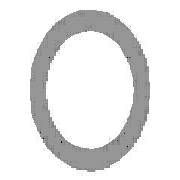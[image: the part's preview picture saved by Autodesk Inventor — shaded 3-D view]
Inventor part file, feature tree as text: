
AUTODESK INVENTOR PART (.ipt)
format: ipt  version: 2024.3 (Build 283343000, 343)  size: 120,320 bytes
history: native  units: mm (DEFAULTED — no unit token found)
features: other x4, sketch x1, plane x1
ambient origin geometry x8: Origin, YZ Plane, XZ Plane, XY Plane, X Axis, Y Axis, Z Axis, Center Point
bodies: Solid1 (feature_tree), Body (feature_tree)
feature tree (6):
  parser-record x1  (decoder bookkeeping rows leaked as tree rows — omitted from the tree; the rows remain in map.json)
  other  "Driven Length"
  other  "Start Plane"
  other  "End Plane"
  sketch  "Sketch3"  dims[d0=42.4mm d1=2.0mm d2=1000.0mm d3=0.0mm d4=-0.0mm d5=1000.0mm d6=90.0deg d7=1000.0mm]
  plane  "Work Plane3"
